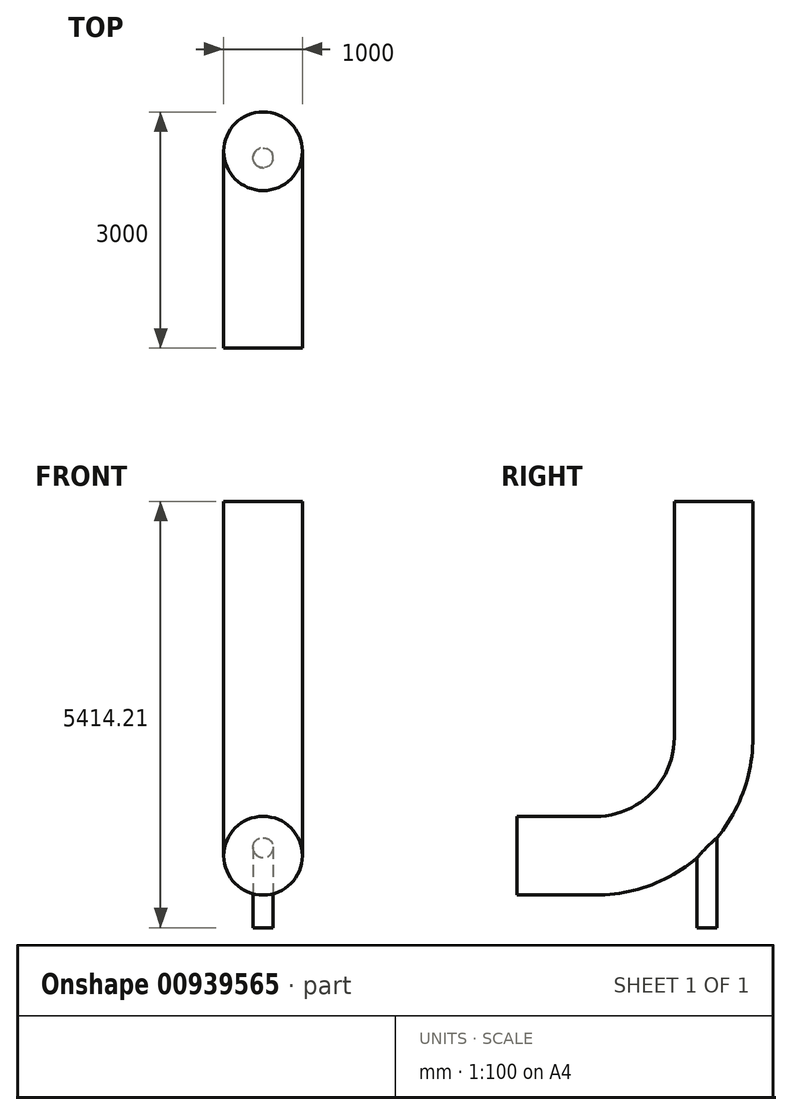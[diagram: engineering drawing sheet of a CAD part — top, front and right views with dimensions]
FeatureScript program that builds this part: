
annotation { "Feature Type Name" : "Feature", "Feature Type Description" : "" }
export const myFeature = defineFeature(function(context is Context, id is Id, definition is map)
    precondition{}
    {
        {
            var Q0;
            Q0=qCreatedBy(makeId("Right.planeOp"),FACE);
            var sketch = newSketch(context, id + "F0", { "sketchPlane" : qUnion([Q0])});
            skLineSegment(sketch, "E0", {"start": v(0, 0) * mm, "end": v(1000, 0) * mm});
            skArc(sketch, "E1", {"start": v(1000, 0) * mm, "mid": v(2060.66, 439.34) * mm, "end": v(2500, 1500) * mm});
            skPoint(sketch, "E2.orphan", {"position": v(1000, 3000) * mm});
            skLineSegment(sketch, "E3", {"start": v(2500, 1500) * mm, "end": v(2500, 4500) * mm});
            skArc(sketch, "E4.0", {"start": v(1000, -500) * mm, "mid": v(2414.21, 85.79) * mm, "end": v(3000, 1500) * mm, "construction": true});
            skLineSegment(sketch, "E5", {"start": v(1000, 0) * mm, "end": v(1000, 1500) * mm, "construction": true});
            skLineSegment(sketch, "E6", {"start": v(1000, 1500) * mm, "end": v(2060.66, 439.34) * mm, "construction": true});
            skLineSegment(sketch, "E7", {"start": v(2414.21, 85.79) * mm, "end": v(2414.21, -914.21) * mm});
            skSolve(sketch);
        }
        {
            var Q0;
            Q0=qCreatedBy(makeId("Front.planeOp"),FACE);
            var sketch = newSketch(context, id + "F1", { "sketchPlane" : qUnion([Q0])});
            skCircle(sketch, "E8", {"center": v(0, 0) * mm, "radius": 500 * mm});
            skSolve(sketch);
        }
        {
            var Q0;
            Q0=makeQuery(id+"F1.imprint","IMPRINT",FACE,{"disambiguationData":[TD([[makeQuery(id+"F1.imprint","IMPRINT",EDGE,{"derivedFrom":sQuery(id+"F1.wireOp",EDGE,"E8")}),1.0]])]});
            var Q1;
            Q1=sQuery(id+"F0.wireOp",EDGE,"E0");
            var Q2;
            Q2=sQuery(id+"F0.wireOp",EDGE,"E1");
            var Q3;
            Q3=sQuery(id+"F0.wireOp",EDGE,"E3");
            sweep(context, id + "F2", {"profiles" : qUnion([Q0]), "path" : qUnion([Q1, Q2, Q3])});
        }
        {
            var Q0;
            Q0=sQuery(id+"F0.wireOp",VERTEX,"E7.end");
            var Q1;
            Q1=sQuery(id+"F0.wireOp",EDGE,"E7");
            cPlane(context, id + "F3", {"entities" : qUnion([Q0, Q1]), "cplaneType" : CPlaneType.LINE_POINT, "offset" : 25.4 * mm, "width" : 152.4 * mm, "height" : 152.4 * mm});
        }
        {
            var Q0;
            Q0=qCreatedBy(id+"F3.planeOp",FACE);
            var sketch = newSketch(context, id + "F4", { "sketchPlane" : qUnion([Q0])});
            skCircle(sketch, "E9", {"center": v(0, -2415.87) * mm, "radius": 127 * mm});
            skSolve(sketch);
        }
        {
            var Q0;
            Q0=makeQuery(id+"F4.imprint","IMPRINT",FACE,{"disambiguationData":[TD([[makeQuery(id+"F4.imprint","IMPRINT",EDGE,{"derivedFrom":sQuery(id+"F4.wireOp",EDGE,"E9")}),1.0]])]});
            extrude(context, id + "F5", {"entities" : qUnion([Q0]), "operationType" : NewBodyOperationType.ADD, "oppositeDirection" : true, "depth" : 1658.62 * mm, "offsetDistance" : 25.4 * mm});
        }
    });
